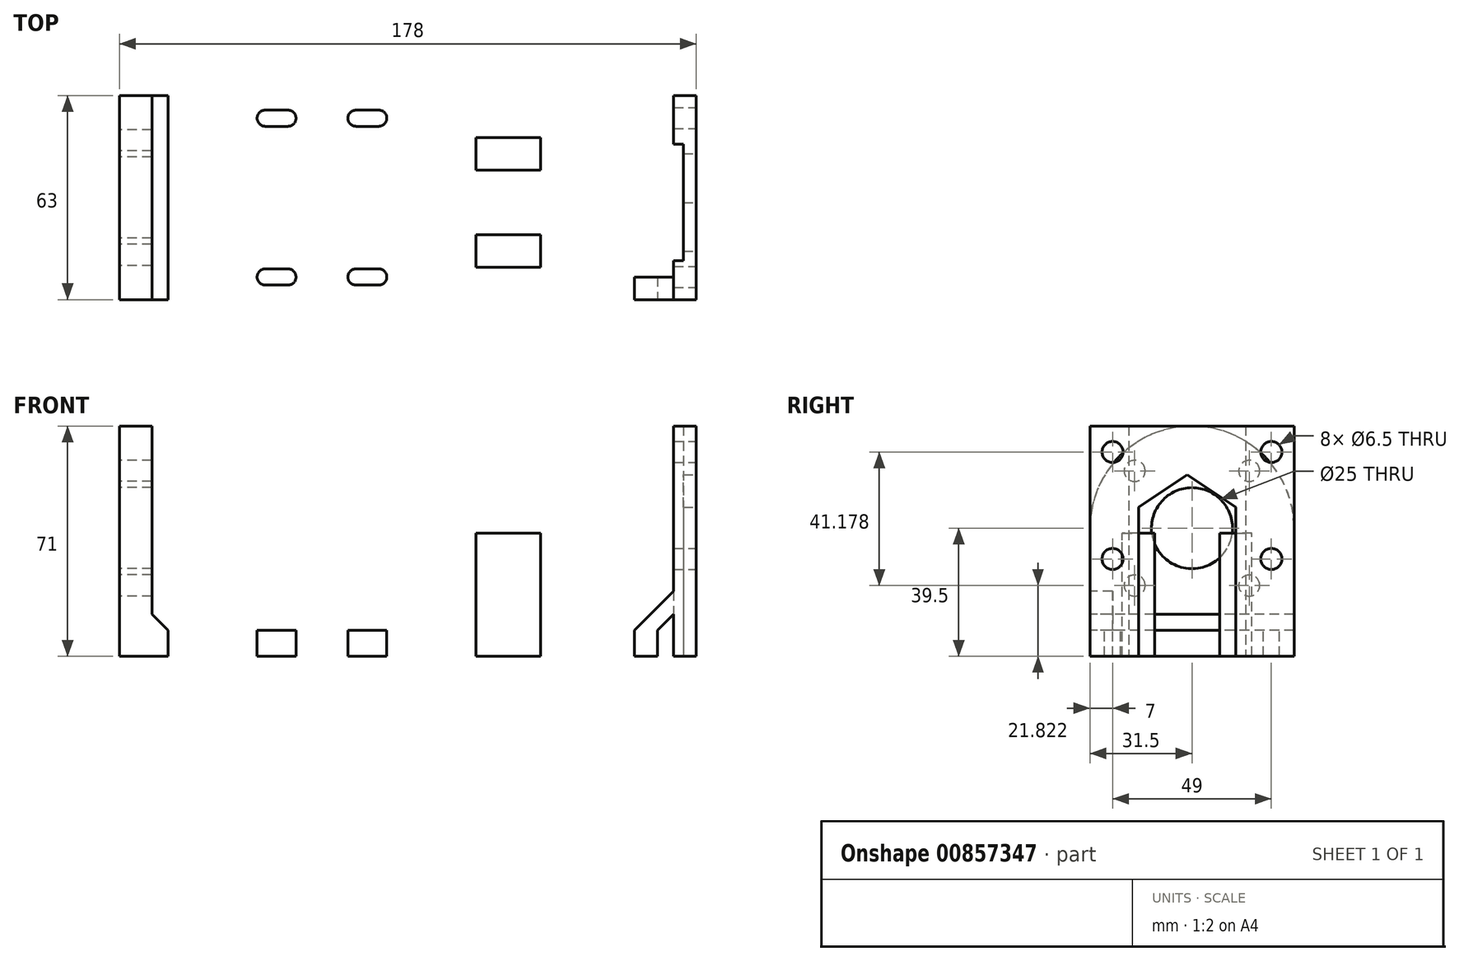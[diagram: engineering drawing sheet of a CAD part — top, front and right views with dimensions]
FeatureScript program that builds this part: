
annotation { "Feature Type Name" : "Feature", "Feature Type Description" : "" }
export const myFeature = defineFeature(function(context is Context, id is Id, definition is map)
    precondition{}
    {
        {
            var Q0;
            Q0=qCreatedBy(makeId("Top.planeOp"),FACE);
            var sketch = newSketch(context, id + "F0", { "sketchPlane" : qUnion([Q0])});
            skLineSegment(sketch, "E0.bottom", {"start": v(-76.5, 31.5) * mm, "end": v(76.5, 31.5) * mm});
            skLineSegment(sketch, "E0.top", {"start": v(-76.5, -31.5) * mm, "end": v(76.5, -31.5) * mm});
            skLineSegment(sketch, "E0.left", {"start": v(-76.5, 31.5) * mm, "end": v(-76.5, -31.5) * mm});
            skPoint(sketch, "E0.middle", {"position": v(0, 0) * mm});
            skLineSegment(sketch, "E1", {"start": v(76.5, 31.5) * mm, "end": v(101.5, 31.5) * mm});
            skLineSegment(sketch, "E2", {"start": v(101.5, 31.5) * mm, "end": v(101.5, -31.5) * mm});
            skLineSegment(sketch, "E3", {"start": v(101.5, -31.5) * mm, "end": v(76.5, -31.5) * mm});
            skSolve(sketch);
        }
        {
            var Q0;
            Q0=makeQuery(id+"F0.imprint","IMPRINT",FACE,{"disambiguationData":[TD([[makeQuery(id+"F0.imprint","IMPRINT",EDGE,{"derivedFrom":sQuery(id+"F0.wireOp",EDGE,"E0.bottom")}),-1.0]])]});
            extrude(context, id + "F1", {"entities" : qUnion([Q0]), "depth" : 8 * mm, "offsetDistance" : 25 * mm});
        }
        {
            var Q0;
            Q0=makeQuery(id+"F1.opExtrude","SWEPT_FACE",FACE,{"disambiguationData":[OSD([sQuery(id+"F0.wireOp",EDGE,"E0.left")])]});
            var sketch = newSketch(context, id + "F2", { "sketchPlane" : qUnion([Q0])});
            skArc(sketch, "E4", {"start": v(31.5, 39.5) * mm, "mid": v(0, 71) * mm, "end": v(-31.5, 39.5) * mm});
            skLineSegment(sketch, "E5", {"start": v(0, 8) * mm, "end": v(0, 39.5) * mm, "construction": true});
            skLineSegment(sketch, "E6", {"start": v(-31.5, 39.5) * mm, "end": v(-31.5, 8) * mm});
            skLineSegment(sketch, "E7", {"start": v(31.5, 39.5) * mm, "end": v(31.5, 8) * mm});
            skLineSegment(sketch, "E8", {"start": v(-31.5, 8) * mm, "end": v(31.5, 8) * mm});
            skCircle(sketch, "E9", {"center": v(0, 39.5) * mm, "radius": 25 * mm, "construction": true});
            skLineSegment(sketch, "E10", {"start": v(0, 39.5) * mm, "end": v(0, 64.5) * mm, "construction": true});
            skLineSegment(sketch, "E11", {"start": v(0, 64.5) * mm, "end": v(-17.68, 57.18) * mm, "construction": true});
            skLineSegment(sketch, "E12", {"start": v(-17.68, 57.18) * mm, "end": v(0, 39.5) * mm, "construction": true});
            skLineSegment(sketch, "E13", {"start": v(0, 39.5) * mm, "end": v(17.68, 57.18) * mm, "construction": true});
            skLineSegment(sketch, "E14", {"start": v(17.68, 57.18) * mm, "end": v(17.68, 21.82) * mm, "construction": true});
            skLineSegment(sketch, "E15", {"start": v(17.68, 21.82) * mm, "end": v(-17.68, 21.82) * mm, "construction": true});
            skLineSegment(sketch, "E16", {"start": v(17.68, 21.82) * mm, "end": v(0, 39.5) * mm, "construction": true});
            skLineSegment(sketch, "E17", {"start": v(0, 39.5) * mm, "end": v(-17.68, 21.82) * mm, "construction": true});
            skCircle(sketch, "E18", {"center": v(-17.68, 57.18) * mm, "radius": 3.25 * mm});
            skCircle(sketch, "E19", {"center": v(17.68, 57.18) * mm, "radius": 3.25 * mm});
            skCircle(sketch, "E20", {"center": v(-17.68, 21.82) * mm, "radius": 3.25 * mm});
            skCircle(sketch, "E21", {"center": v(17.68, 21.82) * mm, "radius": 3.25 * mm});
            skCircle(sketch, "E22", {"center": v(0, 39.5) * mm, "radius": 12.5 * mm});
            skSolve(sketch);
        }
        {
            var Q0;
            Q0=makeQuery(id+"F2.imprint","IMPRINT",FACE,{"disambiguationData":[TD([[makeQuery(id+"F2.imprint","IMPRINT",EDGE,{"derivedFrom":sQuery(id+"F2.wireOp",EDGE,"E4")}),1.0]])]});
            extrude(context, id + "F3", {"entities" : qUnion([Q0]), "operationType" : NewBodyOperationType.ADD, "oppositeDirection" : true, "depth" : 10 * mm, "offsetDistance" : 25 * mm});
        }
        {
            var Q0;
            Q0=makeQuery(id+"F1.opExtrude","CAP_FACE",FACE,{"disambiguationData":[OSD([sQuery(id+"F0.wireOp",EDGE,"E0.bottom"),sQuery(id+"F0.wireOp",EDGE,"E0.top"),sQuery(id+"F0.wireOp",EDGE,"E0.left"),sQuery(id+"F0.wireOp",EDGE,"E1"),sQuery(id+"F0.wireOp",EDGE,"E2"),sQuery(id+"F0.wireOp",EDGE,"E3")])],"isStart":false});
            var sketch = newSketch(context, id + "F4", { "sketchPlane" : qUnion([Q0])});
            skLineSegment(sketch, "E23", {"start": v(-66.5, -31.5) * mm, "end": v(33.5, -31.5) * mm, "construction": true});
            skLineSegment(sketch, "E24", {"start": v(33.5, -31.5) * mm, "end": v(33.5, -21.5) * mm, "construction": true});
            skLineSegment(sketch, "E25", {"start": v(33.5, -21.5) * mm, "end": v(53.5, -21.5) * mm});
            skLineSegment(sketch, "E26", {"start": v(53.5, -21.5) * mm, "end": v(53.5, -11.5) * mm});
            skLineSegment(sketch, "E27", {"start": v(53.5, -11.5) * mm, "end": v(33.5, -11.5) * mm});
            skLineSegment(sketch, "E28", {"start": v(33.5, -11.5) * mm, "end": v(33.5, -21.5) * mm});
            skLineSegment(sketch, "E29", {"start": v(33.5, -11.5) * mm, "end": v(33.5, 8.5) * mm, "construction": true});
            skLineSegment(sketch, "E30", {"start": v(33.5, 8.5) * mm, "end": v(53.5, 8.5) * mm});
            skLineSegment(sketch, "E31", {"start": v(53.5, 8.5) * mm, "end": v(53.5, 18.5) * mm});
            skLineSegment(sketch, "E32", {"start": v(53.5, 18.5) * mm, "end": v(33.5, 18.5) * mm});
            skLineSegment(sketch, "E33", {"start": v(33.5, 18.5) * mm, "end": v(33.5, 8.5) * mm});
            skSolve(sketch);
        }
        {
            var Q0;
            Q0=makeQuery(id+"F4.imprint","IMPRINT",FACE,{"disambiguationData":[TD([[makeQuery(id+"F4.imprint","IMPRINT",EDGE,{"derivedFrom":sQuery(id+"F4.wireOp",EDGE,"E30")}),1.0]])]});
            var Q1;
            Q1=makeQuery(id+"F4.imprint","IMPRINT",FACE,{"disambiguationData":[TD([[makeQuery(id+"F4.imprint","IMPRINT",EDGE,{"derivedFrom":sQuery(id+"F4.wireOp",EDGE,"E25")}),1.0]])]});
            extrude(context, id + "F5", {"entities" : qUnion([Q0, Q1]), "operationType" : NewBodyOperationType.ADD, "depth" : 30 * mm, "offsetDistance" : 25 * mm});
        }
        {
            var Q0;
            Q0=makeQuery(id+"F1.opExtrude","CAP_FACE",FACE,{"disambiguationData":[OSD([sQuery(id+"F0.wireOp",EDGE,"E0.bottom"),sQuery(id+"F0.wireOp",EDGE,"E0.top"),sQuery(id+"F0.wireOp",EDGE,"E0.left"),sQuery(id+"F0.wireOp",EDGE,"E1"),sQuery(id+"F0.wireOp",EDGE,"E2"),sQuery(id+"F0.wireOp",EDGE,"E3")])],"isStart":false});
            var sketch = newSketch(context, id + "F6", { "sketchPlane" : qUnion([Q0])});
            skLineSegment(sketch, "E34", {"start": v(101.5, -31.5) * mm, "end": v(101.5, -16.5) * mm});
            skLineSegment(sketch, "E35", {"start": v(101.5, -16.5) * mm, "end": v(97.5, -16.5) * mm});
            skLineSegment(sketch, "E36", {"start": v(94.5, -19.5) * mm, "end": v(94.5, -31.5) * mm});
            skLineSegment(sketch, "E37", {"start": v(94.5, -31.5) * mm, "end": v(101.5, -31.5) * mm});
            skLineSegment(sketch, "E38", {"start": v(101.5, 31.5) * mm, "end": v(101.5, 13.5) * mm});
            skLineSegment(sketch, "E39", {"start": v(101.5, 13.5) * mm, "end": v(97.5, 13.5) * mm});
            skLineSegment(sketch, "E40", {"start": v(94.5, 16.5) * mm, "end": v(94.5, 31.5) * mm});
            skLineSegment(sketch, "E41", {"start": v(94.5, 31.5) * mm, "end": v(101.5, 31.5) * mm});
            skLineSegment(sketch, "E42", {"start": v(94.5, 16.5) * mm, "end": v(97.5, 16.5) * mm});
            skLineSegment(sketch, "E43", {"start": v(97.5, 16.5) * mm, "end": v(97.5, 13.5) * mm});
            skLineSegment(sketch, "E44", {"start": v(94.5, -19.5) * mm, "end": v(97.5, -19.5) * mm});
            skLineSegment(sketch, "E45", {"start": v(97.5, -19.5) * mm, "end": v(97.5, -16.5) * mm});
            skSolve(sketch);
        }
        {
            var Q0;
            Q0=makeQuery(id+"F6.imprint","IMPRINT",FACE,{"disambiguationData":[TD([[makeQuery(id+"F6.imprint","IMPRINT",EDGE,{"derivedFrom":sQuery(id+"F6.wireOp",EDGE,"E38")}),-1.0]])]});
            var Q1;
            Q1=makeQuery(id+"F6.imprint","IMPRINT",FACE,{"disambiguationData":[TD([[makeQuery(id+"F6.imprint","IMPRINT",EDGE,{"derivedFrom":sQuery(id+"F6.wireOp",EDGE,"E34")}),-1.0]])]});
            extrude(context, id + "F7", {"entities" : qUnion([Q0, Q1]), "operationType" : NewBodyOperationType.ADD, "depth" : 63 * mm, "offsetDistance" : 25 * mm});
        }
        {
            var Q0;
            Q0=makeQuery(id+"F7.boolean.opBoolean","MERGE",FACE,{"derivedFrom":[makeQuery(id+"F1.opExtrude","SWEPT_FACE",FACE,{"disambiguationData":[OSD([sQuery(id+"F0.wireOp",EDGE,"E2")])]}),makeQuery(id+"F7.opExtrude","SWEPT_FACE",FACE,{"disambiguationData":[OSD([sQuery(id+"F6.wireOp",EDGE,"E34")])]}),makeQuery(id+"F7.opExtrude","SWEPT_FACE",FACE,{"disambiguationData":[OSD([sQuery(id+"F6.wireOp",EDGE,"E38")])]})]});
            var sketch = newSketch(context, id + "F8", { "sketchPlane" : qUnion([Q0])});
            skLineSegment(sketch, "E46", {"start": v(-16.5, 71) * mm, "end": v(13.5, 71) * mm});
            skLineSegment(sketch, "E47", {"start": v(13.5, 71) * mm, "end": v(13.5, 46) * mm});
            skLineSegment(sketch, "E48", {"start": v(13.5, 46) * mm, "end": v(-16.5, 46) * mm, "construction": true});
            skLineSegment(sketch, "E49", {"start": v(-16.5, 46) * mm, "end": v(-16.5, 71) * mm});
            skLineSegment(sketch, "E50", {"start": v(-1.5, 46) * mm, "end": v(-1.5, 56) * mm, "construction": true});
            skLineSegment(sketch, "E51", {"start": v(-1.5, 56) * mm, "end": v(-16.5, 46) * mm});
            skLineSegment(sketch, "E52", {"start": v(-1.5, 56) * mm, "end": v(13.5, 46) * mm});
            skSolve(sketch);
        }
        {
            var Q0;
            Q0=makeQuery(id+"F8.imprint","IMPRINT",FACE,{"disambiguationData":[TD([[makeQuery(id+"F8.imprint","IMPRINT",EDGE,{"derivedFrom":sQuery(id+"F8.wireOp",EDGE,"E46")}),-1.0]])]});
            var Q1;
            Q1=makeQuery(id+"F7.opExtrude","SWEPT_FACE",FACE,{"disambiguationData":[OSD([sQuery(id+"F6.wireOp",EDGE,"E43")])]});
            extrude(context, id + "F9", {"entities" : qUnion([Q0]), "operationType" : NewBodyOperationType.ADD, "endBound" : BoundingType.UP_TO_SURFACE, "oppositeDirection" : true, "depth" : 25 * mm, "endBoundEntityFace" : qUnion([Q1]), "offsetDistance" : 25 * mm});
        }
        {
            var Q0;
            Q0=makeQuery(id+"F7.boolean.opBoolean","MERGE",FACE,{"derivedFrom":[makeQuery(id+"F3.boolean.opBoolean","MERGE",FACE,{"derivedFrom":[makeQuery(id+"F1.opExtrude","SWEPT_FACE",FACE,{"disambiguationData":[OSD([sQuery(id+"F0.wireOp",EDGE,"E0.top"),sQuery(id+"F0.wireOp",EDGE,"E3")])]}),makeQuery(id+"F3.opExtrude","SWEPT_FACE",FACE,{"disambiguationData":[OSD([sQuery(id+"F2.wireOp",EDGE,"E7")])]})]}),makeQuery(id+"F7.opExtrude","SWEPT_FACE",FACE,{"disambiguationData":[OSD([sQuery(id+"F6.wireOp",EDGE,"E37")])]})]});
            var sketch = newSketch(context, id + "F10", { "sketchPlane" : qUnion([Q0])});
            skLineSegment(sketch, "E53", {"start": v(94.5, 13) * mm, "end": v(89.5, 8) * mm});
            skLineSegment(sketch, "E54", {"start": v(85.96, 11.54) * mm, "end": v(94.5, 20.07) * mm});
            skLineSegment(sketch, "E55", {"start": v(94.5, 20.07) * mm, "end": v(94.5, 13) * mm});
            skLineSegment(sketch, "E56", {"start": v(85.96, 11.54) * mm, "end": v(82.43, 8) * mm});
            skLineSegment(sketch, "E57", {"start": v(82.43, 8) * mm, "end": v(89.5, 8) * mm});
            skPoint(sketch, "E58.start.orphan", {"position": v(94.5, 8) * mm});
            skSolve(sketch);
        }
        {
            var Q0;
            Q0=makeQuery(id+"F10.imprint","IMPRINT",FACE,{"disambiguationData":[TD([[makeQuery(id+"F10.imprint","IMPRINT",EDGE,{"derivedFrom":sQuery(id+"F10.wireOp",EDGE,"E53")}),-1.0]])]});
            extrude(context, id + "F11", {"entities" : qUnion([Q0]), "operationType" : NewBodyOperationType.ADD, "oppositeDirection" : true, "depth" : 7 * mm, "offsetDistance" : 25 * mm});
        }
        {
            var Q0;
            Q0=makeQuery(id+"F9.boolean.opBoolean","MERGE",FACE,{"derivedFrom":[makeQuery(id+"F7.boolean.opBoolean","MERGE",FACE,{"derivedFrom":[makeQuery(id+"F1.opExtrude","SWEPT_FACE",FACE,{"disambiguationData":[OSD([sQuery(id+"F0.wireOp",EDGE,"E2")])]}),makeQuery(id+"F7.opExtrude","SWEPT_FACE",FACE,{"disambiguationData":[OSD([sQuery(id+"F6.wireOp",EDGE,"E34")])]}),makeQuery(id+"F7.opExtrude","SWEPT_FACE",FACE,{"disambiguationData":[OSD([sQuery(id+"F6.wireOp",EDGE,"E38")])]})]}),makeQuery(id+"F9.opExtrude","CAP_FACE",FACE,{"disambiguationData":[OSD([sQuery(id+"F8.wireOp",EDGE,"E46"),sQuery(id+"F8.wireOp",EDGE,"E47"),sQuery(id+"F8.wireOp",EDGE,"E49"),sQuery(id+"F8.wireOp",EDGE,"E51"),sQuery(id+"F8.wireOp",EDGE,"E52")])],"isStart":true})]});
            var sketch = newSketch(context, id + "F12", { "sketchPlane" : qUnion([Q0])});
            skLineSegment(sketch, "E59", {"start": v(-24.5, 63) * mm, "end": v(-24.5, 30) * mm});
            skLineSegment(sketch, "E60", {"start": v(-24.5, 30) * mm, "end": v(24.5, 30) * mm});
            skLineSegment(sketch, "E61", {"start": v(24.5, 30) * mm, "end": v(24.5, 63) * mm});
            skLineSegment(sketch, "E62", {"start": v(24.5, 63) * mm, "end": v(-24.5, 63) * mm});
            skPoint(sketch, "E63", {"position": v(-24.5, 63) * mm});
            skPoint(sketch, "E64", {"position": v(24.5, 63) * mm});
            skPoint(sketch, "E65", {"position": v(24.5, 30) * mm});
            skPoint(sketch, "E66", {"position": v(-24.5, 30) * mm});
            skSolve(sketch);
        }
        {
            var Q0;
            Q0=sQuery(id+"F12.wireOp",VERTEX,"E63");
            var Q1;
            Q1=sQuery(id+"F12.wireOp",VERTEX,"E64");
            var Q2;
            Q2=sQuery(id+"F12.wireOp",VERTEX,"E65");
            var Q3;
            Q3=sQuery(id+"F12.wireOp",VERTEX,"E66");
            var Q4;
            Q4=makeQuery(id+"F1.opExtrude","SWEPT_BODY",BODY,{"disambiguationData":[OSD([sQuery(id+"F0.wireOp",EDGE,"E0.bottom"),sQuery(id+"F0.wireOp",EDGE,"E0.top"),sQuery(id+"F0.wireOp",EDGE,"E0.left"),sQuery(id+"F0.wireOp",EDGE,"E1"),sQuery(id+"F0.wireOp",EDGE,"E2"),sQuery(id+"F0.wireOp",EDGE,"E3")])]});
            hole(context, id + "F13", {"style" : HoleStyle.SIMPLE, "endStyle" : HoleEndStyle.BLIND, "holeDiameter" : 6.5 * mm, "majorDiameter" : 5 * mm, "holeDepth" : 15 * mm, "isTappedThrough" : true, "tappedDepth" : 12 * mm, "tapClearance" : 3, "locations" : qUnion([Q0, Q1, Q2, Q3]), "scope" : qUnion([Q4])});
        }
        {
            var Q0;
            Q0=makeQuery(id+"F11.boolean.opBoolean","MERGE",FACE,{"derivedFrom":[makeQuery(id+"F7.boolean.opBoolean","MERGE",FACE,{"derivedFrom":[makeQuery(id+"F3.boolean.opBoolean","MERGE",FACE,{"derivedFrom":[makeQuery(id+"F1.opExtrude","SWEPT_FACE",FACE,{"disambiguationData":[OSD([sQuery(id+"F0.wireOp",EDGE,"E0.top"),sQuery(id+"F0.wireOp",EDGE,"E3")])]}),makeQuery(id+"F3.opExtrude","SWEPT_FACE",FACE,{"disambiguationData":[OSD([sQuery(id+"F2.wireOp",EDGE,"E7")])]})]}),makeQuery(id+"F7.opExtrude","SWEPT_FACE",FACE,{"disambiguationData":[OSD([sQuery(id+"F6.wireOp",EDGE,"E37")])]})]}),makeQuery(id+"F11.opExtrude","CAP_FACE",FACE,{"disambiguationData":[OSD([sQuery(id+"F10.wireOp",EDGE,"E53"),sQuery(id+"F10.wireOp",EDGE,"E54"),sQuery(id+"F10.wireOp",EDGE,"E55"),sQuery(id+"F10.wireOp",EDGE,"E56"),sQuery(id+"F10.wireOp",EDGE,"E57")])],"isStart":true})]});
            var sketch = newSketch(context, id + "F14", { "sketchPlane" : qUnion([Q0])});
            skLineSegment(sketch, "E67", {"start": v(-66.5, 8) * mm, "end": v(-66.5, 13) * mm});
            skLineSegment(sketch, "E68", {"start": v(-66.5, 13) * mm, "end": v(-61.5, 8) * mm});
            skLineSegment(sketch, "E69", {"start": v(-61.5, 8) * mm, "end": v(-66.5, 8) * mm});
            skSolve(sketch);
        }
        {
            var Q0;
            Q0=makeQuery(id+"F14.imprint","IMPRINT",FACE,{"disambiguationData":[TD([[makeQuery(id+"F14.imprint","IMPRINT",EDGE,{"derivedFrom":sQuery(id+"F14.wireOp",EDGE,"E67")}),1.0]])]});
            extrude(context, id + "F15", {"entities" : qUnion([Q0]), "operationType" : NewBodyOperationType.ADD, "oppositeDirection" : true, "depth" : 63 * mm, "offsetDistance" : 25 * mm});
        }
        {
            var Q0;
            Q0=makeQuery(id+"F1.opExtrude","CAP_FACE",FACE,{"disambiguationData":[OSD([sQuery(id+"F0.wireOp",EDGE,"E0.bottom"),sQuery(id+"F0.wireOp",EDGE,"E0.top"),sQuery(id+"F0.wireOp",EDGE,"E0.left"),sQuery(id+"F0.wireOp",EDGE,"E1"),sQuery(id+"F0.wireOp",EDGE,"E2"),sQuery(id+"F0.wireOp",EDGE,"E3")])],"isStart":false});
            var sketch = newSketch(context, id + "F16", { "sketchPlane" : qUnion([Q0])});
            skLineSegment(sketch, "E70", {"start": v(101.5, -31.5) * mm, "end": v(3.5, -31.5) * mm, "construction": true});
            skLineSegment(sketch, "E71", {"start": v(3.5, -31.5) * mm, "end": v(3.5, -24.5) * mm, "construction": true});
            skLineSegment(sketch, "E72", {"start": v(3.5, -24.5) * mm, "end": v(-3.5, -24.5) * mm});
            skLineSegment(sketch, "E73", {"start": v(101.5, 31.5) * mm, "end": v(3.5, 31.5) * mm, "construction": true});
            skLineSegment(sketch, "E74", {"start": v(3.5, 31.5) * mm, "end": v(3.5, 24.5) * mm, "construction": true});
            skLineSegment(sketch, "E75", {"start": v(3.5, 24.5) * mm, "end": v(-3.5, 24.5) * mm});
            skLineSegment(sketch, "E76", {"start": v(-3.5, 24.5) * mm, "end": v(-24.5, 24.5) * mm, "construction": true});
            skLineSegment(sketch, "E77", {"start": v(-24.5, 24.5) * mm, "end": v(-31.5, 24.5) * mm});
            skLineSegment(sketch, "E78", {"start": v(-3.5, -24.5) * mm, "end": v(-24.5, -24.5) * mm, "construction": true});
            skLineSegment(sketch, "E79", {"start": v(-24.5, -24.5) * mm, "end": v(-31.5, -24.5) * mm});
            skArc(sketch, "E80.0.startCap", {"start": v(3.5, 27) * mm, "mid": v(6, 24.5) * mm, "end": v(3.5, 22) * mm});
            skArc(sketch, "E80.0.endCap", {"start": v(-3.5, 22) * mm, "mid": v(-6, 24.5) * mm, "end": v(-3.5, 27) * mm});
            skLineSegment(sketch, "E80.0.left", {"start": v(3.5, 22) * mm, "end": v(-3.5, 22) * mm});
            skLineSegment(sketch, "E80.0.right", {"start": v(3.5, 27) * mm, "end": v(-3.5, 27) * mm});
            skArc(sketch, "E80.1.startCap", {"start": v(3.5, -22) * mm, "mid": v(6, -24.5) * mm, "end": v(3.5, -27) * mm});
            skArc(sketch, "E80.1.endCap", {"start": v(-3.5, -27) * mm, "mid": v(-6, -24.5) * mm, "end": v(-3.5, -22) * mm});
            skLineSegment(sketch, "E80.1.left", {"start": v(3.5, -27) * mm, "end": v(-3.5, -27) * mm});
            skLineSegment(sketch, "E80.1.right", {"start": v(3.5, -22) * mm, "end": v(-3.5, -22) * mm});
            skArc(sketch, "E80.2.startCap", {"start": v(-24.5, -22) * mm, "mid": v(-22, -24.5) * mm, "end": v(-24.5, -27) * mm});
            skArc(sketch, "E80.2.endCap", {"start": v(-31.5, -27) * mm, "mid": v(-34, -24.5) * mm, "end": v(-31.5, -22) * mm});
            skLineSegment(sketch, "E80.2.left", {"start": v(-24.5, -27) * mm, "end": v(-31.5, -27) * mm});
            skLineSegment(sketch, "E80.2.right", {"start": v(-24.5, -22) * mm, "end": v(-31.5, -22) * mm});
            skArc(sketch, "E80.3.startCap", {"start": v(-24.5, 27) * mm, "mid": v(-22, 24.5) * mm, "end": v(-24.5, 22) * mm});
            skArc(sketch, "E80.3.endCap", {"start": v(-31.5, 22) * mm, "mid": v(-34, 24.5) * mm, "end": v(-31.5, 27) * mm});
            skLineSegment(sketch, "E80.3.left", {"start": v(-24.5, 22) * mm, "end": v(-31.5, 22) * mm});
            skLineSegment(sketch, "E80.3.right", {"start": v(-24.5, 27) * mm, "end": v(-31.5, 27) * mm});
            skSolve(sketch);
        }
        {
            var Q0;
            Q0=makeQuery(id+"F16.imprint","IMPRINT",FACE,{"disambiguationData":[TD([[makeQuery(id+"F16.imprint","IMPRINT",EDGE,{"derivedFrom":sQuery(id+"F16.wireOp",EDGE,"E80.3.startCap")}),-1.0]])]});
            var Q1;
            Q1=makeQuery(id+"F16.imprint","IMPRINT",FACE,{"disambiguationData":[TD([[makeQuery(id+"F16.imprint","IMPRINT",EDGE,{"derivedFrom":sQuery(id+"F16.wireOp",EDGE,"E80.0.startCap")}),-1.0]])]});
            var Q2;
            Q2=makeQuery(id+"F16.imprint","IMPRINT",FACE,{"disambiguationData":[TD([[makeQuery(id+"F16.imprint","IMPRINT",EDGE,{"derivedFrom":sQuery(id+"F16.wireOp",EDGE,"E80.1.startCap")}),-1.0]])]});
            var Q3;
            Q3=makeQuery(id+"F16.imprint","IMPRINT",FACE,{"disambiguationData":[TD([[makeQuery(id+"F16.imprint","IMPRINT",EDGE,{"derivedFrom":sQuery(id+"F16.wireOp",EDGE,"E80.2.startCap")}),-1.0]])]});
            extrude(context, id + "F17", {"entities" : qUnion([Q0, Q1, Q2, Q3]), "operationType" : NewBodyOperationType.REMOVE, "oppositeDirection" : true, "depth" : 8 * mm, "offsetDistance" : 25 * mm});
        }
        {
            var Q0;
            Q0=makeQuery(id+"F1.opExtrude","CAP_FACE",FACE,{"disambiguationData":[OSD([sQuery(id+"F0.wireOp",EDGE,"E0.bottom"),sQuery(id+"F0.wireOp",EDGE,"E0.top"),sQuery(id+"F0.wireOp",EDGE,"E0.left"),sQuery(id+"F0.wireOp",EDGE,"E1"),sQuery(id+"F0.wireOp",EDGE,"E2"),sQuery(id+"F0.wireOp",EDGE,"E3")])],"isStart":false});
            var sketch = newSketch(context, id + "F18", { "sketchPlane" : qUnion([Q0])});
            skCircle(sketch, "E81.cCircle", {"center": v(-49.5, 11.5) * mm, "radius": 5 * mm, "construction": true});
            skLineSegment(sketch, "E81.0", {"start": v(-52.39, 16.5) * mm, "end": v(-46.61, 16.5) * mm});
            skLineSegment(sketch, "E81.1", {"start": v(-46.61, 16.5) * mm, "end": v(-43.73, 11.5) * mm});
            skLineSegment(sketch, "E81.2", {"start": v(-43.73, 11.5) * mm, "end": v(-46.61, 6.5) * mm});
            skLineSegment(sketch, "E81.3", {"start": v(-46.61, 6.5) * mm, "end": v(-52.39, 6.5) * mm});
            skLineSegment(sketch, "E81.4", {"start": v(-52.39, 6.5) * mm, "end": v(-55.27, 11.5) * mm});
            skLineSegment(sketch, "E81.5", {"start": v(-55.27, 11.5) * mm, "end": v(-52.39, 16.5) * mm});
            skPoint(sketch, "E81.0.midPoint", {"position": v(-49.5, 16.5) * mm});
            skLineSegment(sketch, "E82", {"start": v(-49.5, 11.5) * mm, "end": v(-49.5, 31.5) * mm});
            skLineSegment(sketch, "E83", {"start": v(-49.5, 11.5) * mm, "end": v(-61.5, 11.5) * mm});
            skLineSegment(sketch, "E84.0.1.0", {"start": v(-45.26, -0.98) * mm, "end": v(-42.37, 4.02) * mm});
            skLineSegment(sketch, "E84.0.1.1", {"start": v(-42.37, 4.02) * mm, "end": v(-36.6, 4.02) * mm});
            skLineSegment(sketch, "E84.0.1.2", {"start": v(-36.6, 4.02) * mm, "end": v(-33.71, -0.98) * mm});
            skLineSegment(sketch, "E84.0.1.3", {"start": v(-33.71, -0.98) * mm, "end": v(-36.6, -5.98) * mm});
            skLineSegment(sketch, "E84.0.1.4", {"start": v(-36.6, -5.98) * mm, "end": v(-42.37, -5.98) * mm});
            skLineSegment(sketch, "E84.0.1.5", {"start": v(-42.37, -5.98) * mm, "end": v(-45.26, -0.98) * mm});
            skLineSegment(sketch, "E84.1.0.0", {"start": v(-34.27, 11.5) * mm, "end": v(-31.39, 16.5) * mm});
            skLineSegment(sketch, "E84.1.0.1", {"start": v(-31.39, 16.5) * mm, "end": v(-25.61, 16.5) * mm});
            skLineSegment(sketch, "E84.1.0.2", {"start": v(-25.61, 16.5) * mm, "end": v(-22.73, 11.5) * mm});
            skLineSegment(sketch, "E84.1.0.3", {"start": v(-22.73, 11.5) * mm, "end": v(-25.61, 6.5) * mm});
            skLineSegment(sketch, "E84.1.0.4", {"start": v(-25.61, 6.5) * mm, "end": v(-31.39, 6.5) * mm});
            skLineSegment(sketch, "E84.1.0.5", {"start": v(-31.39, 6.5) * mm, "end": v(-34.27, 11.5) * mm});
            skLineSegment(sketch, "E84.1.1.0", {"start": v(-24.26, -0.98) * mm, "end": v(-21.37, 4.02) * mm});
            skLineSegment(sketch, "E84.1.1.1", {"start": v(-21.37, 4.02) * mm, "end": v(-15.6, 4.02) * mm});
            skLineSegment(sketch, "E84.1.1.2", {"start": v(-15.6, 4.02) * mm, "end": v(-12.71, -0.98) * mm});
            skLineSegment(sketch, "E84.1.1.3", {"start": v(-12.71, -0.98) * mm, "end": v(-15.6, -5.98) * mm});
            skLineSegment(sketch, "E84.1.1.4", {"start": v(-15.6, -5.98) * mm, "end": v(-21.37, -5.98) * mm});
            skLineSegment(sketch, "E84.1.1.5", {"start": v(-21.37, -5.98) * mm, "end": v(-24.26, -0.98) * mm});
            skLineSegment(sketch, "E84.2.0.0", {"start": v(-13.27, 11.5) * mm, "end": v(-10.39, 16.5) * mm});
            skLineSegment(sketch, "E84.2.0.1", {"start": v(-10.39, 16.5) * mm, "end": v(-4.61, 16.5) * mm});
            skLineSegment(sketch, "E84.2.0.2", {"start": v(-4.61, 16.5) * mm, "end": v(-1.73, 11.5) * mm});
            skLineSegment(sketch, "E84.2.0.3", {"start": v(-1.73, 11.5) * mm, "end": v(-4.61, 6.5) * mm});
            skLineSegment(sketch, "E84.2.0.4", {"start": v(-4.61, 6.5) * mm, "end": v(-10.39, 6.5) * mm});
            skLineSegment(sketch, "E84.2.0.5", {"start": v(-10.39, 6.5) * mm, "end": v(-13.27, 11.5) * mm});
            skLineSegment(sketch, "E84.2.1.0", {"start": v(-3.26, -0.98) * mm, "end": v(-0.37, 4.02) * mm});
            skLineSegment(sketch, "E84.2.1.1", {"start": v(-0.37, 4.02) * mm, "end": v(5.4, 4.02) * mm});
            skLineSegment(sketch, "E84.2.1.2", {"start": v(5.4, 4.02) * mm, "end": v(8.29, -0.98) * mm});
            skLineSegment(sketch, "E84.2.1.3", {"start": v(8.29, -0.98) * mm, "end": v(5.4, -5.98) * mm});
            skLineSegment(sketch, "E84.2.1.4", {"start": v(5.4, -5.98) * mm, "end": v(-0.37, -5.98) * mm});
            skLineSegment(sketch, "E84.2.1.5", {"start": v(-0.37, -5.98) * mm, "end": v(-3.26, -0.98) * mm});
            skLineSegment(sketch, "E84.3.0.0", {"start": v(7.73, 11.5) * mm, "end": v(10.61, 16.5) * mm});
            skLineSegment(sketch, "E84.3.0.1", {"start": v(10.61, 16.5) * mm, "end": v(16.39, 16.5) * mm});
            skLineSegment(sketch, "E84.3.0.2", {"start": v(16.39, 16.5) * mm, "end": v(19.27, 11.5) * mm});
            skLineSegment(sketch, "E84.3.0.3", {"start": v(19.27, 11.5) * mm, "end": v(16.39, 6.5) * mm});
            skLineSegment(sketch, "E84.3.0.4", {"start": v(16.39, 6.5) * mm, "end": v(10.61, 6.5) * mm});
            skLineSegment(sketch, "E84.3.0.5", {"start": v(10.61, 6.5) * mm, "end": v(7.73, 11.5) * mm});
            skLineSegment(sketch, "E84.3.1.0", {"start": v(17.74, -0.98) * mm, "end": v(20.63, 4.02) * mm});
            skLineSegment(sketch, "E84.3.1.1", {"start": v(20.63, 4.02) * mm, "end": v(26.4, 4.02) * mm});
            skLineSegment(sketch, "E84.3.1.2", {"start": v(26.4, 4.02) * mm, "end": v(29.29, -0.98) * mm});
            skLineSegment(sketch, "E84.3.1.3", {"start": v(29.29, -0.98) * mm, "end": v(26.4, -5.98) * mm});
            skLineSegment(sketch, "E84.3.1.4", {"start": v(26.4, -5.98) * mm, "end": v(20.63, -5.98) * mm});
            skLineSegment(sketch, "E84.3.1.5", {"start": v(20.63, -5.98) * mm, "end": v(17.74, -0.98) * mm});
            skLineSegment(sketch, "E84.direction1", {"start": v(-55.27, 11.5) * mm, "end": v(-34.27, 11.5) * mm, "construction": true});
            skLineSegment(sketch, "E84.direction2", {"start": v(-55.27, 11.5) * mm, "end": v(-45.26, -0.98) * mm, "construction": true});
            skLineSegment(sketch, "E85.0.1.0", {"start": v(-55.3, -13.5) * mm, "end": v(-52.41, -8.5) * mm});
            skLineSegment(sketch, "E85.0.1.1", {"start": v(-52.41, -8.5) * mm, "end": v(-46.64, -8.5) * mm});
            skLineSegment(sketch, "E85.0.1.2", {"start": v(-46.64, -8.5) * mm, "end": v(-43.75, -13.5) * mm});
            skLineSegment(sketch, "E85.0.1.3", {"start": v(-43.75, -13.5) * mm, "end": v(-46.64, -18.5) * mm});
            skLineSegment(sketch, "E85.0.1.4", {"start": v(-46.64, -18.5) * mm, "end": v(-52.41, -18.5) * mm});
            skLineSegment(sketch, "E85.0.1.5", {"start": v(-52.41, -18.5) * mm, "end": v(-55.3, -13.5) * mm});
            skLineSegment(sketch, "E85.1.1.0", {"start": v(-34.3, -13.5) * mm, "end": v(-31.41, -8.5) * mm});
            skLineSegment(sketch, "E85.1.1.1", {"start": v(-31.41, -8.5) * mm, "end": v(-25.64, -8.5) * mm});
            skLineSegment(sketch, "E85.1.1.2", {"start": v(-25.64, -8.5) * mm, "end": v(-22.75, -13.5) * mm});
            skLineSegment(sketch, "E85.1.1.3", {"start": v(-22.75, -13.5) * mm, "end": v(-25.64, -18.5) * mm});
            skLineSegment(sketch, "E85.1.1.4", {"start": v(-25.64, -18.5) * mm, "end": v(-31.41, -18.5) * mm});
            skLineSegment(sketch, "E85.1.1.5", {"start": v(-31.41, -18.5) * mm, "end": v(-34.3, -13.5) * mm});
            skLineSegment(sketch, "E85.2.1.0", {"start": v(-13.3, -13.5) * mm, "end": v(-10.41, -8.5) * mm});
            skLineSegment(sketch, "E85.2.1.1", {"start": v(-10.41, -8.5) * mm, "end": v(-4.64, -8.5) * mm});
            skLineSegment(sketch, "E85.2.1.2", {"start": v(-4.64, -8.5) * mm, "end": v(-1.75, -13.5) * mm});
            skLineSegment(sketch, "E85.2.1.3", {"start": v(-1.75, -13.5) * mm, "end": v(-4.64, -18.5) * mm});
            skLineSegment(sketch, "E85.2.1.4", {"start": v(-4.64, -18.5) * mm, "end": v(-10.41, -18.5) * mm});
            skLineSegment(sketch, "E85.2.1.5", {"start": v(-10.41, -18.5) * mm, "end": v(-13.3, -13.5) * mm});
            skLineSegment(sketch, "E85.3.1.0", {"start": v(7.7, -13.5) * mm, "end": v(10.59, -8.5) * mm});
            skLineSegment(sketch, "E85.3.1.1", {"start": v(10.59, -8.5) * mm, "end": v(16.36, -8.5) * mm});
            skLineSegment(sketch, "E85.3.1.2", {"start": v(16.36, -8.5) * mm, "end": v(19.25, -13.5) * mm});
            skLineSegment(sketch, "E85.3.1.3", {"start": v(19.25, -13.5) * mm, "end": v(16.36, -18.5) * mm});
            skLineSegment(sketch, "E85.3.1.4", {"start": v(16.36, -18.5) * mm, "end": v(10.59, -18.5) * mm});
            skLineSegment(sketch, "E85.3.1.5", {"start": v(10.59, -18.5) * mm, "end": v(7.7, -13.5) * mm});
            skLineSegment(sketch, "E85.direction2", {"start": v(-55.27, 11.5) * mm, "end": v(-55.3, -13.5) * mm, "construction": true});
            skLineSegment(sketch, "E86.1.0.0", {"start": v(80.63, -5.98) * mm, "end": v(77.74, -0.98) * mm});
            skLineSegment(sketch, "E86.1.0.1", {"start": v(76.36, -8.5) * mm, "end": v(79.25, -13.5) * mm});
            skLineSegment(sketch, "E86.1.0.2", {"start": v(70.61, 16.5) * mm, "end": v(76.39, 16.5) * mm});
            skLineSegment(sketch, "E86.1.0.3", {"start": v(77.74, -0.98) * mm, "end": v(80.63, 4.02) * mm});
            skLineSegment(sketch, "E86.1.0.4", {"start": v(67.73, 11.5) * mm, "end": v(70.61, 16.5) * mm});
            skLineSegment(sketch, "E86.1.0.5", {"start": v(70.59, -18.5) * mm, "end": v(67.7, -13.5) * mm});
            skLineSegment(sketch, "E86.1.0.6", {"start": v(76.39, 16.5) * mm, "end": v(79.27, 11.5) * mm});
            skLineSegment(sketch, "E86.1.0.7", {"start": v(76.36, -18.5) * mm, "end": v(70.59, -18.5) * mm});
            skLineSegment(sketch, "E86.1.0.8", {"start": v(65.4, 4.02) * mm, "end": v(68.29, -0.98) * mm});
            skLineSegment(sketch, "E86.1.0.9", {"start": v(68.29, -0.98) * mm, "end": v(65.4, -5.98) * mm});
            skLineSegment(sketch, "E86.1.0.10", {"start": v(76.39, 6.5) * mm, "end": v(70.61, 6.5) * mm});
            skLineSegment(sketch, "E86.1.0.11", {"start": v(70.59, -8.5) * mm, "end": v(76.36, -8.5) * mm});
            skLineSegment(sketch, "E86.1.0.12", {"start": v(67.7, -13.5) * mm, "end": v(70.59, -8.5) * mm});
            skLineSegment(sketch, "E86.1.0.13", {"start": v(80.63, 4.02) * mm, "end": v(86.4, 4.02) * mm});
            skLineSegment(sketch, "E86.1.0.14", {"start": v(86.4, 4.02) * mm, "end": v(89.29, -0.98) * mm});
            skLineSegment(sketch, "E86.1.0.15", {"start": v(79.25, -13.5) * mm, "end": v(76.36, -18.5) * mm});
            skLineSegment(sketch, "E86.1.0.16", {"start": v(86.4, -5.98) * mm, "end": v(80.63, -5.98) * mm});
            skLineSegment(sketch, "E86.1.0.17", {"start": v(70.61, 6.5) * mm, "end": v(67.73, 11.5) * mm});
            skLineSegment(sketch, "E86.1.0.18", {"start": v(79.27, 11.5) * mm, "end": v(76.39, 6.5) * mm});
            skLineSegment(sketch, "E86.1.0.19", {"start": v(89.29, -0.98) * mm, "end": v(86.4, -5.98) * mm});
            skLineSegment(sketch, "E86.1.0.20", {"start": v(70.61, 6.5) * mm, "end": v(67.73, 11.5) * mm});
            skLineSegment(sketch, "E86.1.0.21", {"start": v(67.73, 11.5) * mm, "end": v(70.61, 16.5) * mm});
            skLineSegment(sketch, "E86.1.0.22", {"start": v(76.39, 16.5) * mm, "end": v(79.27, 11.5) * mm});
            skLineSegment(sketch, "E86.1.0.23", {"start": v(79.27, 11.5) * mm, "end": v(76.39, 6.5) * mm});
            skLineSegment(sketch, "E86.1.0.24", {"start": v(70.61, 16.5) * mm, "end": v(76.39, 16.5) * mm});
            skLineSegment(sketch, "E86.1.0.25", {"start": v(76.39, 6.5) * mm, "end": v(70.61, 6.5) * mm});
            skLineSegment(sketch, "E86.1.0.26", {"start": v(59.63, 4.02) * mm, "end": v(65.4, 4.02) * mm});
            skLineSegment(sketch, "E86.1.0.27", {"start": v(56.74, -0.98) * mm, "end": v(59.63, 4.02) * mm});
            skLineSegment(sketch, "E86.1.0.28", {"start": v(59.63, -5.98) * mm, "end": v(56.74, -0.98) * mm});
            skLineSegment(sketch, "E86.1.0.29", {"start": v(65.4, -5.98) * mm, "end": v(59.63, -5.98) * mm});
            skLineSegment(sketch, "E86.direction1", {"start": v(10.59, -18.5) * mm, "end": v(70.59, -18.5) * mm, "construction": true});
            skLineSegment(sketch, "E87.1.0.0", {"start": v(40.63, -5.98) * mm, "end": v(37.74, -0.98) * mm});
            skLineSegment(sketch, "E87.1.0.1", {"start": v(49.29, -0.98) * mm, "end": v(46.4, -5.98) * mm});
            skLineSegment(sketch, "E87.1.0.2", {"start": v(46.4, -5.98) * mm, "end": v(40.63, -5.98) * mm});
            skLineSegment(sketch, "E87.1.0.3", {"start": v(40.63, 4.02) * mm, "end": v(46.4, 4.02) * mm});
            skLineSegment(sketch, "E87.1.0.4", {"start": v(37.74, -0.98) * mm, "end": v(40.63, 4.02) * mm});
            skLineSegment(sketch, "E87.1.0.5", {"start": v(46.4, 4.02) * mm, "end": v(49.29, -0.98) * mm});
            skLineSegment(sketch, "E87.direction1", {"start": v(20.63, -5.98) * mm, "end": v(40.63, -5.98) * mm, "construction": true});
            skSolve(sketch);
        }
        {
            var Q0;
            Q0 = qSketchRegion(id + "F18", true);
            extrude(context, id + "F19", {"entities" : qUnion([Q0]), "operationType" : NewBodyOperationType.REMOVE, "oppositeDirection" : true, "depth" : 8 * mm, "offsetDistance" : 25 * mm});
        }
    });
